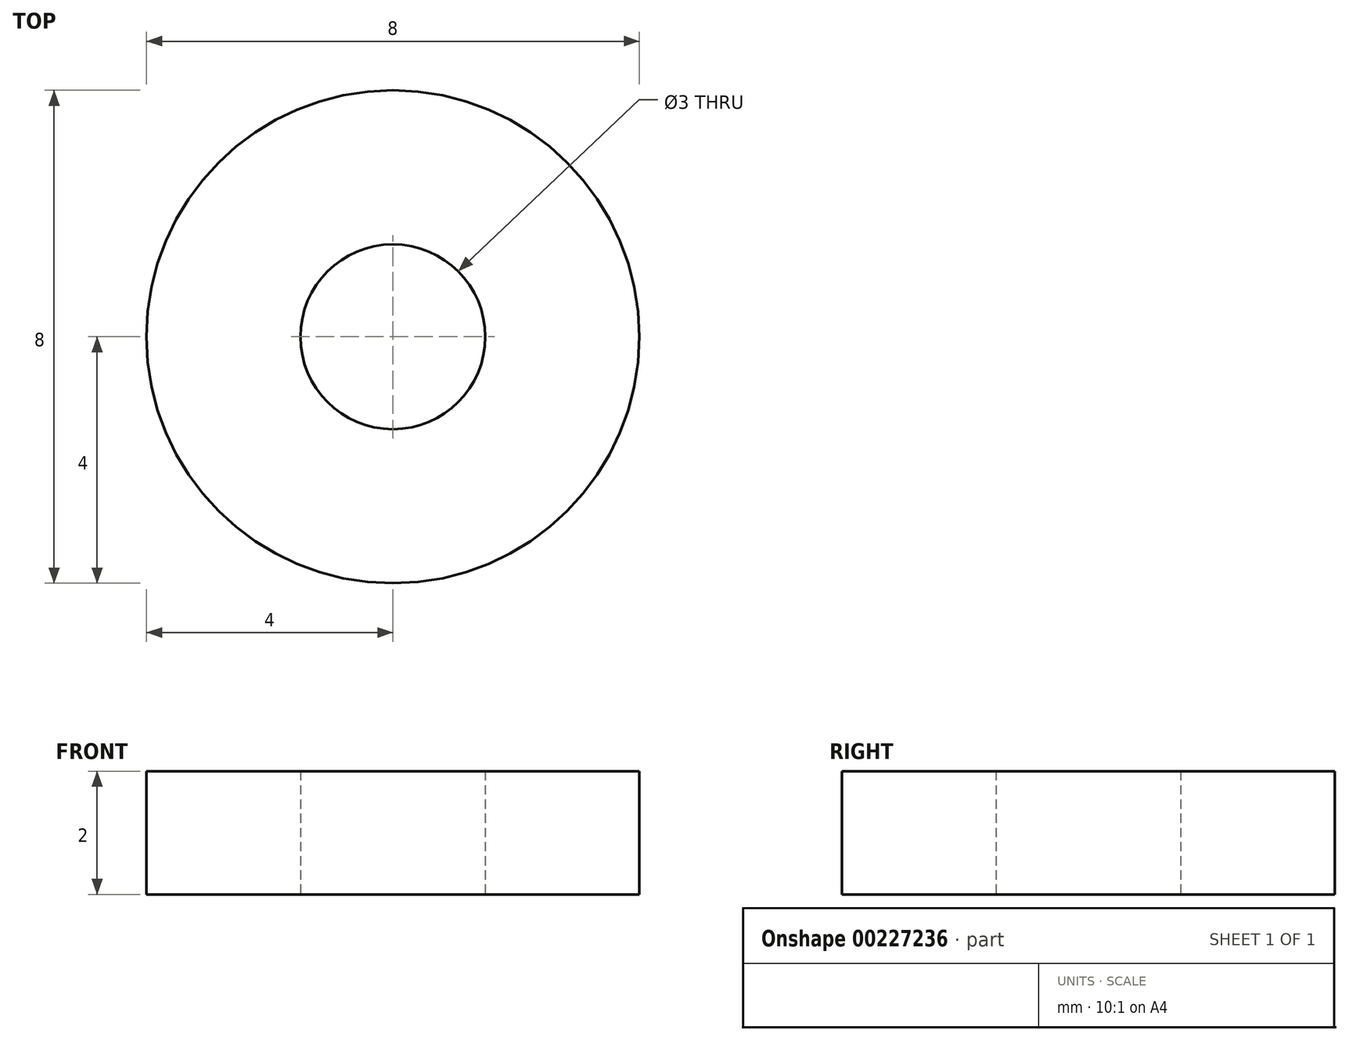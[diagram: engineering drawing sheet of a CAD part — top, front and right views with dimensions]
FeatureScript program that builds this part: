
annotation { "Feature Type Name" : "Feature", "Feature Type Description" : "" }
export const myFeature = defineFeature(function(context is Context, id is Id, definition is map)
    precondition{}
    {
        {
            var Q0;
            Q0=qCreatedBy(makeId("Top.planeOp"),FACE);
            var sketch = newSketch(context, id + "F0", { "sketchPlane" : qUnion([Q0])});
            skCircle(sketch, "E0", {"center": v(0, 0) * mm, "radius": 1.5 * mm});
            skCircle(sketch, "E1", {"center": v(0, 0) * mm, "radius": 4 * mm});
            skSolve(sketch);
        }
        {
            var Q0;
            Q0=makeQuery(id+"F0.imprint","IMPRINT",FACE,{"disambiguationData":[TD([[makeQuery(id+"F0.imprint","IMPRINT",EDGE,{"derivedFrom":sQuery(id+"F0.wireOp",EDGE,"E0")}),-1.0]])]});
            extrude(context, id + "F1", {"entities" : qUnion([Q0]), "depth" : 2 * mm});
        }
    });
